# Revit family: CVB
name_source: partatom
category: Mechanical Equipment
units: mm (PartAtom-declared; Revit-internal decimal feet)

## family parameters
Always vertical = Yes
Cut with Voids When Loaded = No
Part Type = Normal
Room Calculation Point = No
Round Connector Dimension = Use Radius
Shared = No
Work Plane-Based = No

## types (10) — shared parameters
0 = 0' - 0"
1" = 0' - 1"
1.5 = 0' - 1 1/2"
2" = 0' - 2"
2' = 2' - 0"
3" = 0' - 3"
3/16 = 0' - 0 3/16"
3/4 = 0' - 0 3/4"
4" = 0' - 4"
Manufacturer = Loren Cook Company
Model = CVB
ONE EIGTH = 0' - 0 1/8"
T_SQ = 2' - 8"
T_SQ/2 = 1' - 4"
Type Comments = Centri-Vane All Aluminum Inline Centrifugal Blower Belt Drive
URL = www.lorencook.com

## per-type parameters (varying)
| type | (-B/2)+.125" | (-B/2)+.25" | (A/2)+E | (C/2)-E | (F/2)-1" | (G/2)-1" | A | A/2 | A/4 | B | B/2 | C | C+F | C+F-1" | C/2 | D | D+(A/2)+E+F | E | F | F/3 | G | G/2 | H | H/2 |
| 10_CVB | -0' - 7 3/8" | -0' - 7 1/4" | 0' - 6 5/16" | 0' - 6 25/32" | 0' - 5 1/2" | 0' - 5 1/8" | 0' - 10" | 0' - 5" | 0' - 2 1/2" | 1' - 3" | 0' - 7 1/2" | 1' - 4 3/16" | 2' - 3 7/16" | 2' - 2 7/16" | 0' - 8 3/32" | 0' - 8 11/16" | 2' - 2 1/4" | 0' - 1 5/16" | 0' - 11 1/4" | 0' - 3 3/4" | 1' - 0 1/4" | 0' - 6 1/8" | 1' - 1" | 0' - 6 1/2" |
| 12_CVB | -0' - 8 7/16" | -0' - 8 5/16" | 0' - 7 5/16" | 0' - 8 1/4" | 0' - 6 9/16" | 0' - 6 1/16" | 1' - 0" | 0' - 6" | 0' - 3" | 1' - 5 1/8" | 0' - 8 9/16" | 1' - 7 1/8" | 2' - 6 3/8" | 2' - 5 3/8" | 0' - 9 9/16" | 0' - 9 15/16" | 2' - 4 1/2" | 0' - 1 5/16" | 0' - 11 1/4" | 0' - 3 3/4" | 1' - 2 1/8" | 0' - 7 1/16" | 1' - 3 1/8" | 0' - 7 9/16" |
| 14_CVB | -0' - 9 7/16" | -0' - 9 5/16" | 0' - 8 5/16" | 0' - 9 11/16" | 0' - 7 9/16" | 0' - 7 1/8" | 1' - 2" | 0' - 7" | 0' - 3 1/2" | 1' - 7 1/8" | 0' - 9 9/16" | 1' - 10" | 2' - 9 1/4" | 2' - 8 1/4" | 0' - 11" | 0' - 11 7/16" | 2' - 7" | 0' - 1 5/16" | 0' - 11 1/4" | 0' - 3 3/4" | 1' - 4 1/4" | 0' - 8 1/8" | 1' - 5 1/8" | 0' - 8 9/16" |
| 16_CVB | -0' - 10 21/32" | -0' - 10 17/32" | 0' - 9 5/16" | 0' - 11 1/8" | 0' - 8 25/32" | 0' - 8 1/8" | 1' - 4" | 0' - 8" | 0' - 4" | 1' - 9 9/16" | 0' - 10 25/32" | 2' - 0 7/8" | 3' - 0 1/8" | 2' - 11 1/8" | 1' - 0 7/16" | 1' - 0 11/16" | 2' - 9 1/4" | 0' - 1 5/16" | 0' - 11 1/4" | 0' - 3 3/4" | 1' - 6 1/4" | 0' - 9 1/8" | 1' - 7 9/16" | 0' - 9 25/32" |
| 18_CVB | -1' - 0 1/8" | -1' - 0" | 0' - 10 5/16" | 1' - 0 9/16" | 0' - 10 1/4" | 0' - 9 3/16" | 1' - 6" | 0' - 9" | 0' - 4 1/2" | 2' - 0 1/2" | 1' - 0 1/4" | 2' - 3 3/4" | 3' - 3" | 3' - 2" | 1' - 1 7/8" | 1' - 2" | 2' - 11 9/16" | 0' - 1 5/16" | 0' - 11 1/4" | 0' - 3 3/4" | 1' - 8 3/8" | 0' - 10 3/16" | 1' - 10 1/2" | 0' - 11 1/4" |
| 20_CVB | -1' - 1 1/16" | -1' - 0 15/16" | 0' - 11 5/16" | 1' - 1 15/16" | 0' - 11 3/16" | 0' - 10 1/4" | 1' - 8" | 0' - 10" | 0' - 5" | 2' - 2 3/8" | 1' - 1 3/16" | 2' - 6 1/2" | 3' - 7 3/4" | 3' - 6 3/4" | 1' - 3 1/4" | 1' - 3 3/4" | 3' - 4 5/16" | 0' - 1 5/16" | 1' - 1 1/4" | 0' - 4 13/32" | 1' - 10 1/2" | 0' - 11 1/4" | 2' - 0 3/8" | 1' - 0 3/16" |
| 24_CVB | -1' - 3 1/2" | -1' - 3 3/8" | 1' - 1 9/16" | 1' - 4 11/16" | 1' - 1 5/8" | 1' - 0 3/8" | 2' - 0" | 1' - 0" | 0' - 6" | 2' - 7 1/4" | 1' - 3 5/8" | 3' - 0 1/2" | 4' - 1 3/4" | 4' - 0 3/4" | 1' - 6 1/4" | 1' - 6 5/8" | 3' - 9 7/16" | 0' - 1 9/16" | 1' - 1 1/4" | 0' - 4 13/32" | 2' - 2 3/4" | 1' - 1 3/8" | 2' - 5 1/4" | 1' - 2 5/8" |
| 28_CVB | -1' - 5 7/8" | -1' - 5 3/4" | 1' - 3 9/16" | 1' - 7 7/16" | 1' - 4" | 1' - 2 3/8" | 2' - 4" | 1' - 2" | 0' - 7" | 3' - 0" | 1' - 6" | 3' - 6" | 4' - 9 1/2" | 4' - 8 1/2" | 1' - 9" | 1' - 9 1/2" | 4' - 4 9/16" | 0' - 1 9/16" | 1' - 3 1/2" | 0' - 5 5/32" | 2' - 6 3/4" | 1' - 3 3/8" | 2' - 10" | 1' - 5" |
| 32_CVB | -1' - 8 5/16" | -1' - 8 3/16" | 1' - 5 9/16" | 1' - 10 7/16" | 1' - 6 7/16" | 1' - 4 19/32" | 2' - 8" | 1' - 4" | 0' - 8" | 3' - 4 7/8" | 1' - 8 7/16" | 4' - 0" | 5' - 3 1/2" | 5' - 2 1/2" | 2' - 0" | 2' - 0 7/16" | 4' - 9 1/2" | 0' - 1 9/16" | 1' - 3 1/2" | 0' - 5 5/32" | 2' - 11 3/16" | 1' - 5 19/32" | 3' - 2 7/8" | 1' - 7 7/16" |
| 36_CVB | -1' - 10" | -1' - 9 7/8" | 1' - 7 9/16" | 2' - 1 1/8" | 1' - 8 1/8" | 1' - 6 11/16" | 3' - 0" | 1' - 6" | 0' - 9" | 3' - 8 1/4" | 1' - 10 1/8" | 4' - 5 3/8" | 5' - 8 7/8" | 5' - 7 7/8" | 2' - 2 11/16" | 2' - 2 3/4" | 5' - 1 13/16" | 0' - 1 9/16" | 1' - 3 1/2" | 0' - 5 5/32" | 3' - 3 3/8" | 1' - 7 11/16" | 3' - 6 1/4" | 1' - 9 1/8" |

## geometry (parser evidence)
native form markers: Sweep x1
no freeform markers — native parametric forms only
